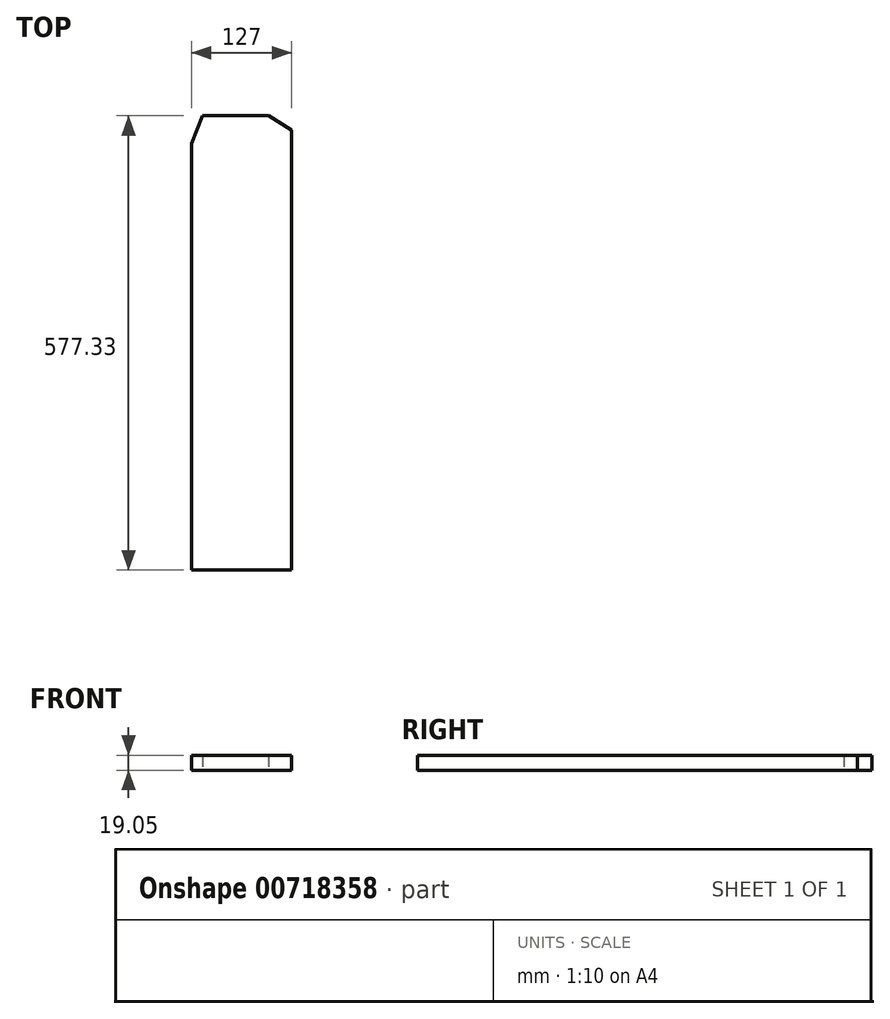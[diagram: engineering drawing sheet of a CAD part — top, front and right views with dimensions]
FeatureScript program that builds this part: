
annotation { "Feature Type Name" : "Feature", "Feature Type Description" : "" }
export const myFeature = defineFeature(function(context is Context, id is Id, definition is map)
    precondition{}
    {
        {
            var Q0;
            Q0=qCreatedBy(makeId("Top.planeOp"),FACE);
            var sketch = newSketch(context, id + "F0", { "sketchPlane" : qUnion([Q0])});
            skLineSegment(sketch, "E0.top", {"start": v(-35.32, -213.66) * mm, "end": v(91.68, -213.66) * mm});
            skLineSegment(sketch, "E0.left", {"start": v(-35.32, 328.15) * mm, "end": v(-35.32, -213.66) * mm});
            skLineSegment(sketch, "E0.right", {"start": v(91.68, 345.14) * mm, "end": v(91.68, -213.66) * mm});
            skPoint(sketch, "E1.end.orphan", {"position": v(55.47, 357) * mm});
            skLineSegment(sketch, "E2", {"start": v(-35.32, 328.15) * mm, "end": v(-21.53, 363.67) * mm});
            skLineSegment(sketch, "E3", {"start": v(-21.53, 363.67) * mm, "end": v(62.32, 363.67) * mm});
            skLineSegment(sketch, "E4", {"start": v(62.32, 363.67) * mm, "end": v(91.68, 345.14) * mm});
            skSolve(sketch);
        }
        {
            var Q0;
            Q0=makeQuery(id+"F0.imprint","IMPRINT",FACE,{"disambiguationData":[TD([[makeQuery(id+"F0.imprint","IMPRINT",EDGE,{"derivedFrom":sQuery(id+"F0.wireOp",EDGE,"E0.bottom")}),-1.0]])]});
            var Q1;
            Q1=makeQuery(id+"F0.imprint","IMPRINT",FACE,{"disambiguationData":[TD([[makeQuery(id+"F0.imprint","IMPRINT",EDGE,{"derivedFrom":sQuery(id+"F0.wireOp",EDGE,"E0.top")}),1.0]])]});
            extrude(context, id + "F1", {"entities" : qUnion([Q0, Q1]), "depth" : 19.05 * mm, "offsetDistance" : 25.4 * mm});
        }
    });
